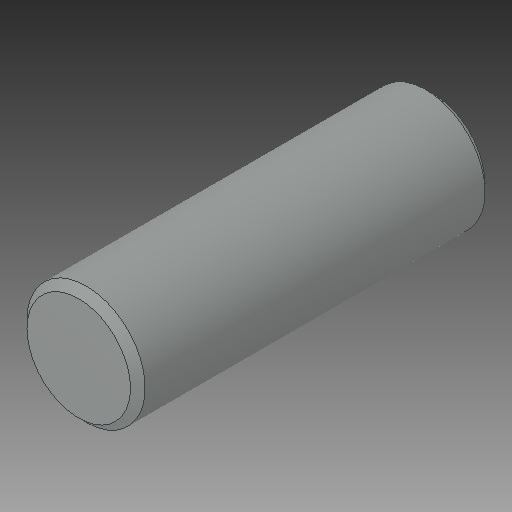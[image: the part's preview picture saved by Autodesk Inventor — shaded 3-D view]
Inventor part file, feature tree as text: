
AUTODESK INVENTOR PART (.ipt)
format: ipt  version: 2017 (Build 210142000, 142)  size: 97,792 bytes
history: native  units: in
note: dims shown in document units (in); Inventor stores cm internally (conversion verified against a paired STEP export)
features: chamfer x1
ambient origin geometry x8: Origin, YZ Plane, XZ Plane, XY Plane, X Axis, Y Axis, Z Axis, Center Point
bodies: Solid1 (feature_tree)
feature tree (1):
  chamfer  "Chamfer1"  [1 undecoded]
note: 1 required parameter value undecoded (feature->parameter linkage not recoverable at this tier; creation-order binding heuristic only, values carry confidence <= 0.55)
